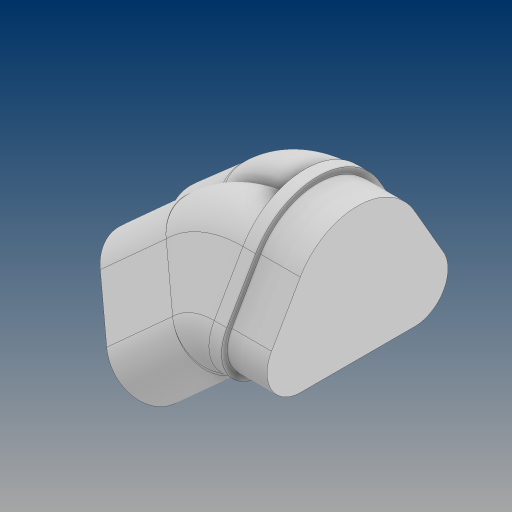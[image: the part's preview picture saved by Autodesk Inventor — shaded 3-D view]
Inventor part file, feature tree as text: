
AUTODESK INVENTOR PART (.ipt)
format: ipt  version: 2023 (Build 270158000, 158)  size: 643,584 bytes
history: native  units: mm
features: extrude x17, sketch x16, revolve x4, plane x2, mirror x2, fillet x1, chamfer x1
ambient origin geometry x8: Origin, YZ Plane, XZ Plane, XY Plane, X Axis, Y Axis, Z Axis, Center Point
bodies: Solid1 (feature_tree)
feature tree (43):
  sketch  "Sketch1"  dims[d0=25.0mm d1=50.0mm]
  revolve  "Revolution1"  [1 undecoded]
  sketch  "Sketch2"  dims[d2=7.5mm d4=15.0mm]
  plane  "Work Plane1"
  sketch  "Sketch4"  dims[d5=11.0mm d6=11.0mm]
  plane  "Work Plane2"
  sketch  "Sketch5"  dims[d7=60.0deg d8=11.0mm]
  revolve  "Revolution2"  [1 undecoded]
  sketch  "Sketch6"  dims[d9=15.0mm d10=45.0deg]
  extrude  "Extrusion2"  Depth=11.0mm
  extrude  "Extrusion3"  Depth=11.0mm
  sketch  "Sketch7"  dims[d11=90.0deg d12=150.0deg]
  revolve  "Revolution3"  Angle=45.0deg
  revolve  "Revolution4"  Angle=150.0deg
  extrude  "Extrusion7"  Depth=39.75mm
  extrude  "Extrusion8"  Depth=15.0mm
  mirror  "Mirror1"
  sketch  "Sketch12"  dims[d15=12.73686mm d20=15.0mm]
  sketch  "Sketch15"  dims[d21=11.0mm d22=90.0deg]
  extrude  "Extrusion12"  TaperAngle=90.0deg  [1 undecoded]
  extrude  "Extrusion13"  TaperAngle=0.0deg  [1 undecoded]
  extrude  "Extrusion14"  TaperAngle=0.0deg  [1 undecoded]
  sketch  "Sketch16"  dims[d23=12.736803mm d24=0.0mm]
  extrude  "Extrusion15"  Depth=1.134464mm
  extrude  "Extrusion16"  Depth=11.0mm
  extrude  "Extrusion17"  Depth=2.0mm
  extrude  "Extrusion18"  Depth=2.0mm
  fillet  "Fillet2"  Radius=6.5mm
  sketch  "Sketch20"  dims[d41=2.0mm d42=2.0mm]
  extrude  "Extrusion27"  Depth=7.6mm TaperAngle=0.0deg
  chamfer  "Chamfer5"  Distance=11.0mm
  extrude  "Extrusion28"  Depth=7.6mm
  mirror  "Mirror3"
  extrude  "Extrusion29"  Depth=7.6mm
  extrude  "Extrusion31"  Depth=7.6mm
  extrude  "Extrusion32"  Depth=7.6mm
  extrude  "Extrusion33"  Depth=7.6mm
  sketch  "Sketch8"  dims[d13=20.5mm d14=39.75mm]
  sketch  "Sketch17"  dims[d25=3.59315mm d26=0.0mm]
  sketch  "Sketch18"  dims[d27=15.0mm d28=1.134464mm]
  sketch  "Sketch19"  dims[d39=11.0mm d40=11.0mm]
  sketch  "Sketch24"  dims[d43=2.0mm d44=2.0mm d47=6.5mm]
  sketch  "Sketch25"  dims[d48=2.0mm d49=0.0mm d50=321.5mm d51=0.0mm d52=11.0mm d53=11.0mm d54=6.5mm d55=6.5mm d56=15.0mm d57=7.5mm d58=60.0deg d59=7.5mm d60=90.0deg d61=1.134464mm d62=15.0mm d63=15.0mm d64=11.0mm d65=11.0mm d66=7.5mm d67=120.0deg d68=7.5mm d69=90.0deg d70=7.5mm d71=120.0deg d72=45.0deg d114=275.0mm d115=100.0mm d116=50.0mm d122=15.0mm d123=0.0mm d124=15.0mm d125=0.0mm d143=25.0mm d144=100.0mm d145=10.0mm d146=90.0deg d147=12.736803mm d148=90.0deg d149=15.0mm d150=5.5mm d151=7.5mm d152=7.5mm d153=2.0mm d154=0.0mm d155=12.0mm d156=0.0mm d157=1.0mm d158=0.0mm d166=550.0mm d167=300.0mm d168=20.0mm d169=15.0mm d170=15.0mm d171=15.0mm d172=15.0mm d173=15.0mm d174=7.5mm d175=7.5mm d176=7.5mm d177=15.0mm d178=35.0mm d179=0.0mm d180=100.0mm d181=0.0mm d182=15.0mm d183=15.0mm d184=15.0mm d185=15.0mm d186=7.5mm d187=7.5mm d188=1.1mm d189=7.6mm d190=0.0mm d191=19.5mm d192=0.0mm d193=0.75mm d194=50.0mm d195=100.0mm d196=300.0mm d198=20.0mm d201=10.0mm d202=2.0mm d241=0.5mm d242=0.5mm d265=70.0mm d267=15.0mm d268=15.0mm d269=15.0mm d270=15.0mm d271=12.8mm d272=12.8mm d273=12.8mm d274=1.0mm d275=1.0mm d276=2.0mm d277=30.0mm d278=2.0mm d279=30.0mm d280=2.0mm d281=40.595mm d282=2.5mm d283=300.0mm d284=0.0mm d285=2.0mm d286=4.0mm d287=45.0deg d288=25.0mm d289=50.0mm d290=10.0mm d291=0.0mm d292=100.0mm d293=0.0mm d294=1.1mm d295=1.1mm d298=7.6mm d299=0.0mm d300=10.025mm d301=0.0mm d302=7.6mm d303=0.0mm d34=0.5mm d35=0.872665mm d36=0.5mm d37=0.872665mm d90=0.5mm d91=0.872665mm d92=0.5mm d93=0.872665mm d160=0.5mm d161=0.872665mm d162=0.5mm d163=0.872665mm d213=0.5mm d214=0.872665mm d215=0.5mm d216=0.872665mm d296=0.0mm d297=0.0mm]
note: 5 required parameter values undecoded (feature->parameter linkage not recoverable at this tier; creation-order binding heuristic only, values carry confidence <= 0.55)